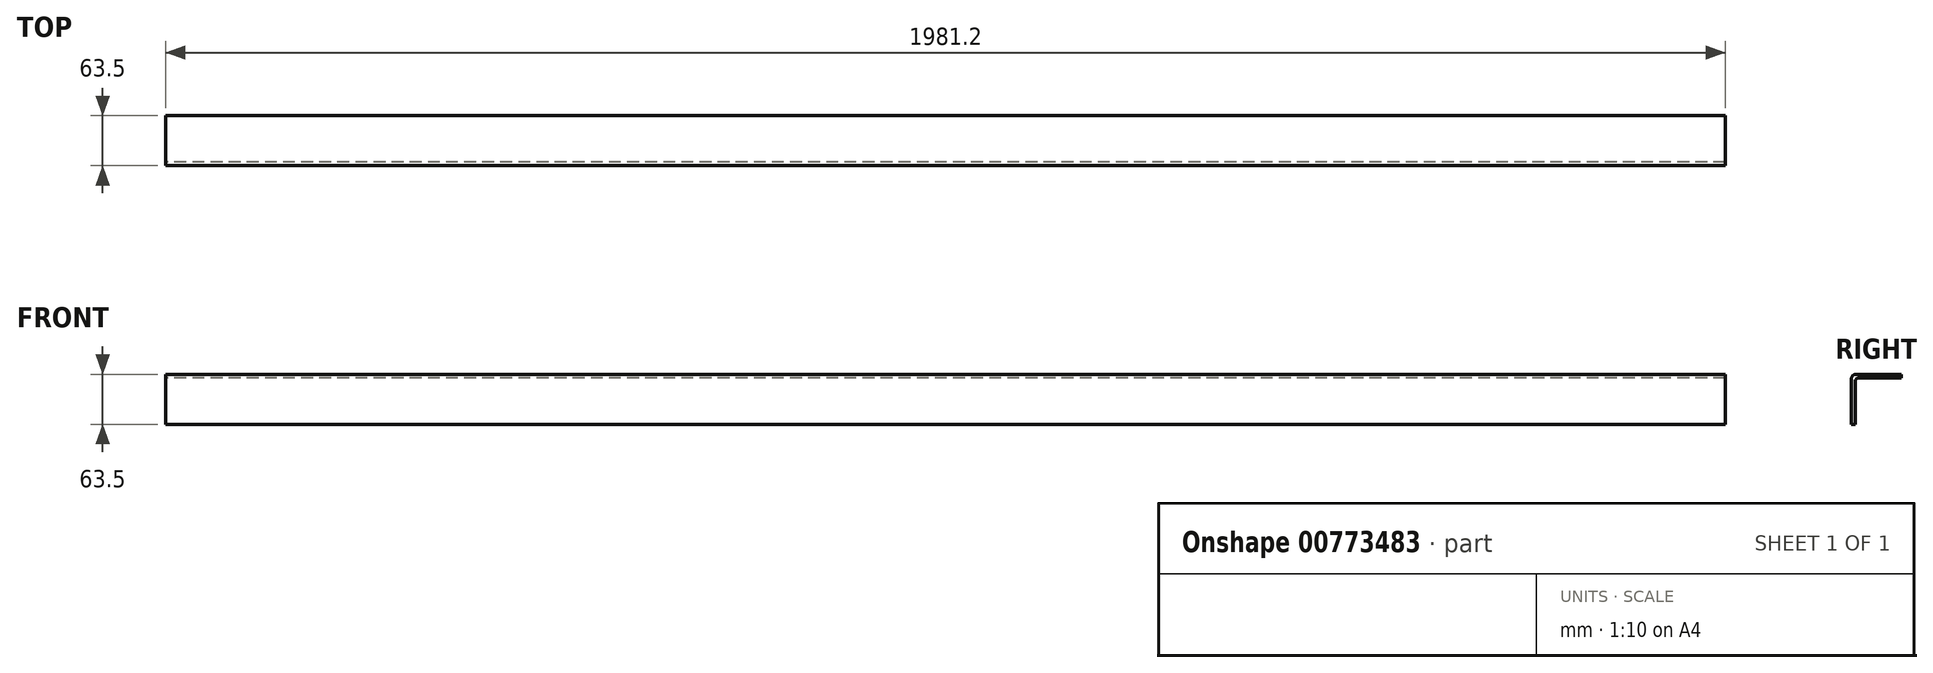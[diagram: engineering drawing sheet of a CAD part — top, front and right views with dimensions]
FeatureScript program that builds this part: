
annotation { "Feature Type Name" : "Feature", "Feature Type Description" : "" }
export const myFeature = defineFeature(function(context is Context, id is Id, definition is map)
    precondition{}
    {
        {
            var Q0;
            Q0=qCreatedBy(makeId("Right.planeOp"),FACE);
            var sketch = newSketch(context, id + "F0", { "sketchPlane" : qUnion([Q0])});
            skLineSegment(sketch, "E0", {"start": v(-28.12, -12.25) * mm, "end": v(-28.12, 44.9) * mm});
            skLineSegment(sketch, "E1", {"start": v(-21.77, 51.25) * mm, "end": v(35.38, 51.25) * mm});
            skPoint(sketch, "E2.visualSharp", {"position": v(-28.12, 51.25) * mm});
            skArc(sketch, "E2.filletArc", {"start": v(-21.77, 51.25) * mm, "mid": v(-26.26, 49.39) * mm, "end": v(-28.12, 44.9) * mm});
            skLineSegment(sketch, "E3", {"start": v(-28.12, -12.25) * mm, "end": v(-23.35, -12.25) * mm});
            skLineSegment(sketch, "E4", {"start": v(35.38, 51.25) * mm, "end": v(35.38, 46.48) * mm});
            skLineSegment(sketch, "E5", {"start": v(-23.35, -12.25) * mm, "end": v(-23.35, 41.4) * mm});
            skLineSegment(sketch, "E6", {"start": v(35.38, 46.48) * mm, "end": v(-18.27, 46.48) * mm});
            skPoint(sketch, "E7.newPointA", {"position": v(-23.35, 46.42) * mm});
            skPoint(sketch, "E7.newPointB", {"position": v(-23.29, 46.48) * mm});
            skArc(sketch, "E7.filletArc", {"start": v(-18.27, 46.48) * mm, "mid": v(-21.87, 45) * mm, "end": v(-23.35, 41.4) * mm});
            skSolve(sketch);
        }
        {
            var Q0;
            Q0=qSketchRegion(id+"F0",true);
            extrude(context, id + "F1", {"entities" : qUnion([Q0]), "depth" : 1981.2 * mm, "offsetDistance" : 25.4 * mm});
        }
    });
